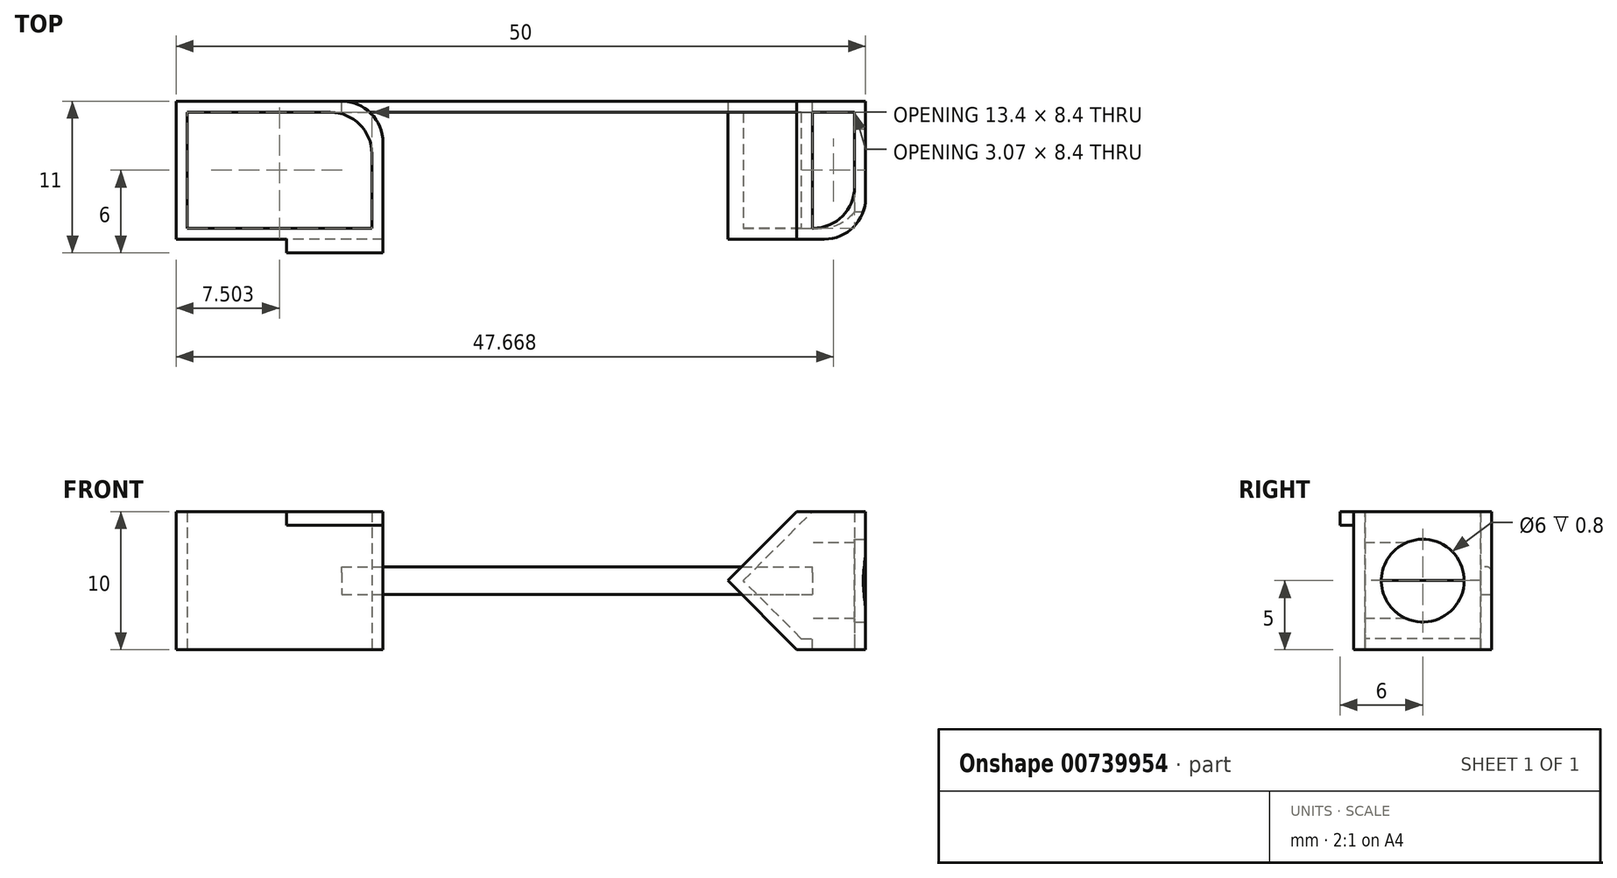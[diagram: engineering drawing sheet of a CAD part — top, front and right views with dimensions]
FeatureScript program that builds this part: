
annotation { "Feature Type Name" : "Feature", "Feature Type Description" : "" }
export const myFeature = defineFeature(function(context is Context, id is Id, definition is map)
    precondition{}
    {
        {
            var Q0;
            Q0=qCreatedBy(makeId("Top.planeOp"),FACE);
            var sketch = newSketch(context, id + "F0", { "sketchPlane" : qUnion([Q0])});
            skLineSegment(sketch, "E0.bottom", {"start": v(-5.53, 10) * mm, "end": v(9.47, 10) * mm});
            skLineSegment(sketch, "E0.top", {"start": v(-5.53, 0) * mm, "end": v(9.47, 0) * mm});
            skLineSegment(sketch, "E0.left", {"start": v(-5.53, 10) * mm, "end": v(-5.53, 0) * mm});
            skLineSegment(sketch, "E0.right", {"start": v(9.47, 10) * mm, "end": v(9.47, 0) * mm});
            skLineSegment(sketch, "E1.bottom", {"start": v(39.47, 10) * mm, "end": v(44.47, 10) * mm});
            skLineSegment(sketch, "E1.top", {"start": v(39.47, 0) * mm, "end": v(44.47, 0) * mm});
            skLineSegment(sketch, "E1.left", {"start": v(39.47, 10) * mm, "end": v(39.47, 0) * mm});
            skLineSegment(sketch, "E1.right", {"start": v(44.47, 10) * mm, "end": v(44.47, 0) * mm});
            skSolve(sketch);
        }
        {
            var Q0;
            Q0 = qSketchRegion(id + "F0", true);
            extrude(context, id + "F1", {"entities" : qUnion([Q0]), "depth" : 10 * mm, "offsetDistance" : 25 * mm});
        }
        {
            var Q0;
            Q0=makeQuery(id+"F1.opExtrude","SWEPT_FACE",FACE,{"disambiguationData":[OSD([sQuery(id+"F0.wireOp",EDGE,"E1.top")])]});
            var sketch = newSketch(context, id + "F2", { "sketchPlane" : qUnion([Q0])});
            skLineSegment(sketch, "E2", {"start": v(39.47, 0) * mm, "end": v(34.47, 5) * mm});
            skLineSegment(sketch, "E3", {"start": v(34.47, 5) * mm, "end": v(39.47, 10) * mm});
            skLineSegment(sketch, "E4", {"start": v(39.47, 10) * mm, "end": v(39.47, 0) * mm});
            skSolve(sketch);
        }
        {
            var Q0;
            Q0 = qSketchRegion(id + "F2", true);
            var Q1;
            Q1=makeQuery(id+"F1.opExtrude","SWEPT_FACE",FACE,{"disambiguationData":[OSD([sQuery(id+"F0.wireOp",EDGE,"E1.bottom")])]});
            extrude(context, id + "F3", {"entities" : qUnion([Q0]), "operationType" : NewBodyOperationType.ADD, "endBound" : BoundingType.UP_TO_SURFACE, "oppositeDirection" : true, "depth" : 15 * mm, "endBoundEntityFace" : qUnion([Q1]), "offsetDistance" : 25 * mm});
        }
        {
            var Q0;
            Q0=makeQuery(id+"F1.opExtrude","CAP_FACE",FACE,{"disambiguationData":[OSD([sQuery(id+"F0.wireOp",EDGE,"E0.bottom"),sQuery(id+"F0.wireOp",EDGE,"E0.top"),sQuery(id+"F0.wireOp",EDGE,"E0.left"),sQuery(id+"F0.wireOp",EDGE,"E0.right")])],"isStart":false});
            var Q1;
            Q1=makeQuery(id+"F1.opExtrude","CAP_FACE",FACE,{"disambiguationData":[OSD([sQuery(id+"F0.wireOp",EDGE,"E1.bottom"),sQuery(id+"F0.wireOp",EDGE,"E1.top"),sQuery(id+"F0.wireOp",EDGE,"E1.left"),sQuery(id+"F0.wireOp",EDGE,"E1.right")])],"isStart":false});
            shell(context, id + "F4", {"entities" : qUnion([Q0, Q1]), "thickness" : 0.8 * mm});
        }
        {
            var Q0;
            Q0=makeQuery(id+"F1.opExtrude","SWEPT_FACE",FACE,{"disambiguationData":[OSD([sQuery(id+"F0.wireOp",EDGE,"E0.left")])]});
            var sketch = newSketch(context, id + "F5", { "sketchPlane" : qUnion([Q0])});
            skLineSegment(sketch, "E5", {"start": v(-4.43, 3.07) * mm, "end": v(-1.55, 5.95) * mm});
            skLineSegment(sketch, "E6", {"start": v(-9.4, 5.95) * mm, "end": v(-4.43, 3.07) * mm});
            skLineSegment(sketch, "E7", {"start": v(-1.55, 5.95) * mm, "end": v(-9.4, 5.95) * mm});
            skSolve(sketch);
        }
        {
            var Q0;
            Q0=makeQuery(id+"F4.opShell","OFFSET_FACE",FACE,{"disambiguationData":[OSD([sQuery(id+"F0.wireOp",EDGE,"E0.bottom"),sQuery(id+"F0.wireOp",EDGE,"E0.top"),sQuery(id+"F0.wireOp",EDGE,"E0.left"),sQuery(id+"F0.wireOp",EDGE,"E0.right")])]});
            var sketch = newSketch(context, id + "F6", { "sketchPlane" : qUnion([Q0])});
            skLineSegment(sketch, "E8.0.0", {"start": v(-4.73, 9.2) * mm, "end": v(-4.73, 0.8) * mm});
            skLineSegment(sketch, "E8.0.1", {"start": v(-4.73, 0.8) * mm, "end": v(8.67, 0.8) * mm});
            skLineSegment(sketch, "E8.0.2", {"start": v(8.67, 0.8) * mm, "end": v(8.67, 9.2) * mm});
            skLineSegment(sketch, "E8.0.3", {"start": v(8.67, 9.2) * mm, "end": v(-4.73, 9.2) * mm});
            skSolve(sketch);
        }
        {
            var Q0;
            Q0 = qSketchRegion(id + "F6", true);
            extrude(context, id + "F7", {"entities" : qUnion([Q0]), "operationType" : NewBodyOperationType.REMOVE, "endBound" : BoundingType.SYMMETRIC, "oppositeDirection" : true, "depth" : 4 * mm, "offsetDistance" : 25 * mm});
        }
        {
            var Q0;
            Q0=makeQuery(id+"F4.opShell","OFFSET_FACE",FACE,{"disambiguationData":[OSD([sQuery(id+"F0.wireOp",EDGE,"E1.bottom"),sQuery(id+"F0.wireOp",EDGE,"E1.top"),sQuery(id+"F0.wireOp",EDGE,"E1.left"),sQuery(id+"F0.wireOp",EDGE,"E1.right")])]});
            var sketch = newSketch(context, id + "F8", { "sketchPlane" : qUnion([Q0])});
            skLineSegment(sketch, "E9.0", {"start": v(40.6, 9.2) * mm, "end": v(43.67, 9.2) * mm});
            skLineSegment(sketch, "E10.0", {"start": v(40.6, 9.2) * mm, "end": v(40.6, 0.8) * mm});
            skLineSegment(sketch, "E11.0", {"start": v(40.6, 0.8) * mm, "end": v(43.67, 0.8) * mm});
            skLineSegment(sketch, "E12.0", {"start": v(43.67, 9.2) * mm, "end": v(43.67, 0.8) * mm});
            skSolve(sketch);
        }
        {
            var Q0;
            Q0 = qSketchRegion(id + "F8", true);
            extrude(context, id + "F9", {"entities" : qUnion([Q0]), "operationType" : NewBodyOperationType.REMOVE, "endBound" : BoundingType.SYMMETRIC, "oppositeDirection" : true, "depth" : 5 * mm, "offsetDistance" : 25 * mm});
        }
        {
            var Q0;
            Q0=makeQuery(id+"F1.opExtrude","SWEPT_FACE",FACE,{"disambiguationData":[OSD([sQuery(id+"F0.wireOp",EDGE,"E1.right")])]});
            var sketch = newSketch(context, id + "F10", { "sketchPlane" : qUnion([Q0])});
            skLineSegment(sketch, "E13", {"start": v(0, 10) * mm, "end": v(10, 0) * mm, "construction": true});
            skLineSegment(sketch, "E14", {"start": v(10, 0) * mm, "end": v(0, 0) * mm, "construction": true});
            skLineSegment(sketch, "E15", {"start": v(0, 0) * mm, "end": v(10, 10) * mm, "construction": true});
            skCircle(sketch, "E16", {"center": v(5, 5) * mm, "radius": 3 * mm});
            skSolve(sketch);
        }
        {
            var Q0;
            Q0=makeQuery(id+"F10.imprint","IMPRINT",FACE,{"disambiguationData":[TD([[makeQuery(id+"F10.imprint","IMPRINT",EDGE,{"derivedFrom":sQuery(id+"F10.wireOp",EDGE,"E16")}),1.0]])]});
            extrude(context, id + "F11", {"entities" : qUnion([Q0]), "operationType" : NewBodyOperationType.REMOVE, "endBound" : BoundingType.SYMMETRIC, "oppositeDirection" : true, "depth" : 5 * mm, "offsetDistance" : 25 * mm});
        }
        {
            var Q0;
            Q0=makeQuery(id+"F3.boolean.opBoolean","MERGE",FACE,{"derivedFrom":[makeQuery(id+"F1.opExtrude","SWEPT_FACE",FACE,{"disambiguationData":[OSD([sQuery(id+"F0.wireOp",EDGE,"E1.top")])]}),makeQuery(id+"F3.opExtrude","CAP_FACE",FACE,{"disambiguationData":[OSD([sQuery(id+"F2.wireOp",EDGE,"E2"),sQuery(id+"F2.wireOp",EDGE,"E3"),sQuery(id+"F2.wireOp",EDGE,"E4")])],"isStart":true})]});
            var sketch = newSketch(context, id + "F12", { "sketchPlane" : qUnion([Q0])});
            skLineSegment(sketch, "E17", {"start": v(30.47, 3) * mm, "end": v(42.47, 3) * mm});
            skLineSegment(sketch, "E18", {"start": v(42.47, 3) * mm, "end": v(39.47, 8.2) * mm});
            skLineSegment(sketch, "E19", {"start": v(39.47, 8.2) * mm, "end": v(30.47, 3) * mm});
            skSolve(sketch);
        }
        {
            var Q0;
            Q0=makeQuery(id+"F3.boolean.opBoolean","MERGE",FACE,{"derivedFrom":[makeQuery(id+"F1.opExtrude","SWEPT_FACE",FACE,{"disambiguationData":[OSD([sQuery(id+"F0.wireOp",EDGE,"E1.bottom")])]}),makeQuery(id+"F3.opExtrude","CAP_FACE",FACE,{"disambiguationData":[OSD([sQuery(id+"F2.wireOp",EDGE,"E2"),sQuery(id+"F2.wireOp",EDGE,"E3"),sQuery(id+"F2.wireOp",EDGE,"E4")])],"isStart":false})]});
            var sketch = newSketch(context, id + "F13", { "sketchPlane" : qUnion([Q0])});
            skLineSegment(sketch, "E20.bottom", {"start": v(-42.97, 8) * mm, "end": v(-30.97, 8) * mm});
            skLineSegment(sketch, "E20.top", {"start": v(-42.97, 2) * mm, "end": v(-30.97, 2) * mm});
            skLineSegment(sketch, "E20.left", {"start": v(-42.97, 8) * mm, "end": v(-42.97, 2) * mm});
            skLineSegment(sketch, "E20.right", {"start": v(-30.97, 8) * mm, "end": v(-30.97, 2) * mm});
            skLineSegment(sketch, "E21", {"start": v(-42.97, 3) * mm, "end": v(-40.97, 3) * mm});
            skLineSegment(sketch, "E22", {"start": v(-40.97, 3) * mm, "end": v(-40.97, 4) * mm});
            skLineSegment(sketch, "E23", {"start": v(-40.97, 4) * mm, "end": v(-38.97, 4) * mm});
            skLineSegment(sketch, "E24", {"start": v(-38.97, 4) * mm, "end": v(-38.97, 5) * mm});
            skLineSegment(sketch, "E25", {"start": v(-38.97, 5) * mm, "end": v(-36.97, 5) * mm});
            skLineSegment(sketch, "E26", {"start": v(-36.97, 5) * mm, "end": v(-36.97, 6) * mm});
            skLineSegment(sketch, "E27", {"start": v(-36.97, 6) * mm, "end": v(-34.97, 6) * mm});
            skLineSegment(sketch, "E28", {"start": v(-34.97, 6) * mm, "end": v(-34.97, 7) * mm});
            skLineSegment(sketch, "E29", {"start": v(-34.97, 7) * mm, "end": v(-32.97, 7) * mm});
            skLineSegment(sketch, "E30", {"start": v(-32.97, 7) * mm, "end": v(-32.97, 8) * mm});
            skSolve(sketch);
        }
        {
            var Q0;
            Q0=makeQuery(id+"F1.opExtrude","SWEPT_EDGE",EDGE,{"disambiguationData":[OSD([sQuery(id+"F0.wireOp",EDGE,"E0.bottom"),sQuery(id+"F0.wireOp",EDGE,"E0.right")])]});
            var Q1;
            Q1=makeQuery(id+"F7.boolean.opBoolean","MERGE",EDGE,{"derivedFrom":[makeQuery(id+"F4.opShell","OFFSET_EDGE",EDGE,{"disambiguationData":[OSD([sQuery(id+"F0.wireOp",EDGE,"E0.bottom"),sQuery(id+"F0.wireOp",EDGE,"E0.right")])]}),makeQuery(id+"F7.opExtrude","SWEPT_EDGE",EDGE,{"disambiguationData":[OSD([sQuery(id+"F6.wireOp",EDGE,"E8.0.2"),sQuery(id+"F6.wireOp",EDGE,"E8.0.3")])]})]});
            var Q2;
            Q2=makeQuery(id+"F1.opExtrude","SWEPT_EDGE",EDGE,{"disambiguationData":[OSD([sQuery(id+"F0.wireOp",EDGE,"E1.top"),sQuery(id+"F0.wireOp",EDGE,"E1.right")])]});
            var Q3;
            Q3=makeQuery(id+"F9.boolean.opBoolean","MERGE",EDGE,{"derivedFrom":[makeQuery(id+"F4.opShell","OFFSET_EDGE",EDGE,{"disambiguationData":[OSD([sQuery(id+"F0.wireOp",EDGE,"E1.top"),sQuery(id+"F0.wireOp",EDGE,"E1.right")])]}),makeQuery(id+"F9.opExtrude","SWEPT_EDGE",EDGE,{"disambiguationData":[OSD([sQuery(id+"F8.wireOp",EDGE,"E11.0"),sQuery(id+"F8.wireOp",EDGE,"E12.0")])]})]});
            fillet(context, id + "F14", {"entities" : qUnion([Q0, Q1, Q2, Q3]), "radius" : 3 * mm, "tangentPropagation" : true, "allowEdgeOverflow" : false});
        }
        {
            var Q0;
            Q0=makeQuery(id+"F1.opExtrude","SWEPT_FACE",FACE,{"disambiguationData":[OSD([sQuery(id+"F0.wireOp",EDGE,"E0.top")])]});
            var sketch = newSketch(context, id + "F15", { "sketchPlane" : qUnion([Q0])});
            skLineSegment(sketch, "E31.bottom", {"start": v(9.47, 10) * mm, "end": v(2.47, 10) * mm});
            skLineSegment(sketch, "E31.top", {"start": v(9.47, 9) * mm, "end": v(2.47, 9) * mm});
            skLineSegment(sketch, "E31.left", {"start": v(9.47, 10) * mm, "end": v(9.47, 9) * mm});
            skLineSegment(sketch, "E31.right", {"start": v(2.47, 10) * mm, "end": v(2.47, 9) * mm});
            skSolve(sketch);
        }
        {
            var Q0;
            Q0 = qSketchRegion(id + "F15", true);
            extrude(context, id + "F16", {"entities" : qUnion([Q0]), "operationType" : NewBodyOperationType.ADD, "depth" : 1 * mm, "offsetDistance" : 25 * mm});
        }
        {
            var Q0;
            Q0=qCreatedBy(makeId("Top.planeOp"),FACE);
            var sketch = newSketch(context, id + "F17", { "sketchPlane" : qUnion([Q0])});
            skLineSegment(sketch, "E32.bottom", {"start": v(6.47, 9.2) * mm, "end": v(40.6, 9.2) * mm});
            skLineSegment(sketch, "E32.top", {"start": v(6.47, 10) * mm, "end": v(40.6, 10) * mm});
            skLineSegment(sketch, "E32.left", {"start": v(6.47, 9.2) * mm, "end": v(6.47, 10) * mm});
            skLineSegment(sketch, "E32.right", {"start": v(40.6, 9.2) * mm, "end": v(40.6, 10) * mm});
            skSolve(sketch);
        }
        {
            var Q0;
            Q0=makeQuery(id+"F17.imprint","IMPRINT",FACE,{"disambiguationData":[TD([[makeQuery(id+"F17.imprint","IMPRINT",EDGE,{"derivedFrom":sQuery(id+"F17.wireOp",EDGE,"E32.bottom")}),1.0]])]});
            extrude(context, id + "F18", {"entities" : qUnion([Q0]), "depth" : 6 * mm, "offsetDistance" : 25 * mm, "hasSecondDirection" : true, "secondDirectionOppositeDirection" : false, "secondDirectionDepth" : 4 * mm});
        }
        {
            var Q0;
            Q0=makeQuery(id+"F18.opExtrude","CAP_EDGE",EDGE,{"disambiguationData":[OSD([sQuery(id+"F17.wireOp",EDGE,"E32.top")])],"isStart":false});
            var Q1;
            Q1=makeQuery(id+"F18.opExtrude","CAP_EDGE",EDGE,{"disambiguationData":[OSD([sQuery(id+"F17.wireOp",EDGE,"E32.bottom")])],"isStart":false});
            fillet(context, id + "F19", {"entities" : qUnion([Q0, Q1]), "radius" : 0.4 * mm, "tangentPropagation" : true, "allowEdgeOverflow" : false});
        }
    });
